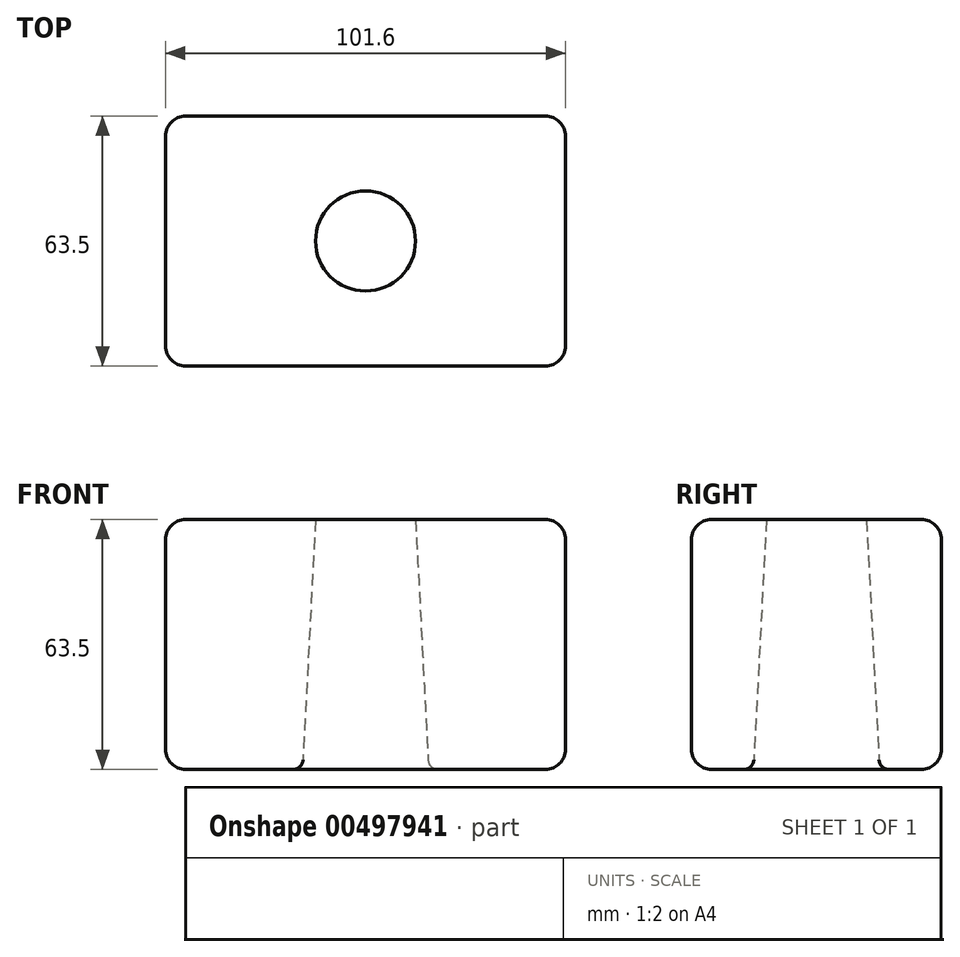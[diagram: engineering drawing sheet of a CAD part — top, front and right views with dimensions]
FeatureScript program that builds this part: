
annotation { "Feature Type Name" : "Feature", "Feature Type Description" : "" }
export const myFeature = defineFeature(function(context is Context, id is Id, definition is map)
    precondition{}
    {
        {
            var Q0;
            Q0=qCreatedBy(makeId("Top.planeOp"),FACE);
            var sketch = newSketch(context, id + "F0", { "sketchPlane" : qUnion([Q0])});
            skLineSegment(sketch, "E0.bottom", {"start": v(50.8, 31.75) * mm, "end": v(-50.8, 31.75) * mm});
            skLineSegment(sketch, "E0.top", {"start": v(50.8, -31.75) * mm, "end": v(-50.8, -31.75) * mm});
            skLineSegment(sketch, "E0.left", {"start": v(50.8, 31.75) * mm, "end": v(50.8, -31.75) * mm});
            skLineSegment(sketch, "E0.right", {"start": v(-50.8, 31.75) * mm, "end": v(-50.8, -31.75) * mm});
            skPoint(sketch, "E0.middle", {"position": v(0, 0) * mm});
            skSolve(sketch);
        }
        {
            var Q0;
            Q0 = qSketchRegion(id + "F0", true);
            extrude(context, id + "F1", {"entities" : qUnion([Q0]), "endBound" : BoundingType.SYMMETRIC, "depth" : 63.5 * mm});
        }
        {
            var Q0;
            Q0=makeQuery(id+"F1.opExtrude","CAP_FACE",FACE,{"disambiguationData":[OSD([sQuery(id+"F0.wireOp",EDGE,"E0.bottom"),sQuery(id+"F0.wireOp",EDGE,"E0.top"),sQuery(id+"F0.wireOp",EDGE,"E0.left"),sQuery(id+"F0.wireOp",EDGE,"E0.right"),sQuery(id+"F0.wireOp",EDGE,"gUM4WlBC-VqhS-AEsS-gTAw-i3EQ8ykjMu5x")])],"isStart":false});
            var Q1;
            Q1=makeQuery(id+"F1.opExtrude","SWEPT_FACE",FACE,{"disambiguationData":[OSD([sQuery(id+"F0.wireOp",EDGE,"E0.top")])]});
            var Q2;
            Q2=makeQuery(id+"F1.opExtrude","SWEPT_FACE",FACE,{"disambiguationData":[OSD([sQuery(id+"F0.wireOp",EDGE,"E0.right")])]});
            var Q3;
            Q3=makeQuery(id+"F1.opExtrude","CAP_FACE",FACE,{"disambiguationData":[OSD([sQuery(id+"F0.wireOp",EDGE,"E0.bottom"),sQuery(id+"F0.wireOp",EDGE,"E0.top"),sQuery(id+"F0.wireOp",EDGE,"E0.left"),sQuery(id+"F0.wireOp",EDGE,"E0.right"),sQuery(id+"F0.wireOp",EDGE,"gUM4WlBC-VqhS-AEsS-gTAw-i3EQ8ykjMu5x")])],"isStart":true});
            var Q4;
            Q4=makeQuery(id+"F1.opExtrude","SWEPT_FACE",FACE,{"disambiguationData":[OSD([sQuery(id+"F0.wireOp",EDGE,"E0.left")])]});
            fillet(context, id + "F2", {"entities" : qUnion([Q0, Q1, Q2, Q3, Q4]), "radius" : 5.08 * mm, "tangentPropagation" : true, "allowEdgeOverflow" : false});
        }
        {
            var Q0;
            Q0=makeQuery(id+"F1.opExtrude","CAP_FACE",FACE,{"disambiguationData":[OSD([sQuery(id+"F0.wireOp",EDGE,"E0.bottom"),sQuery(id+"F0.wireOp",EDGE,"E0.top"),sQuery(id+"F0.wireOp",EDGE,"E0.left"),sQuery(id+"F0.wireOp",EDGE,"E0.right")])],"isStart":false});
            var sketch = newSketch(context, id + "F3", { "sketchPlane" : qUnion([Q0])});
            skCircle(sketch, "E1", {"center": v(0, 0) * mm, "radius": 12.7 * mm});
            skSolve(sketch);
        }
        {
            var Q0;
            Q0 = qSketchRegion(id + "F3", true);
            extrude(context, id + "F4", {"entities" : qUnion([Q0]), "operationType" : NewBodyOperationType.REMOVE, "oppositeDirection" : true, "depth" : 86.87 * mm, "hasDraft" : true, "draftAngle" : 3 * degree});
        }
        {
            var Q0;
            Q0=makeQuery(id+"F4.boolean.opBoolean","COPY",EDGE,{"derivedFrom":makeQuery(id+"F4.opExtrude","CAP_EDGE",EDGE,{"disambiguationData":[OSD([sQuery(id+"F3.wireOp",EDGE,"E1")])],"isStart":true})});
            var Q1;
            Q1=makeQuery(id+"F4.boolean.opBoolean","INTERSECT",EDGE,{"derivedFrom":[makeQuery(id+"F1.opExtrude","CAP_FACE",FACE,{"disambiguationData":[OSD([sQuery(id+"F0.wireOp",EDGE,"E0.bottom"),sQuery(id+"F0.wireOp",EDGE,"E0.top"),sQuery(id+"F0.wireOp",EDGE,"E0.left"),sQuery(id+"F0.wireOp",EDGE,"E0.right")])],"isStart":true}),makeQuery(id+"F4.opExtrude","SWEPT_FACE",FACE,{"disambiguationData":[OSD([sQuery(id+"F3.wireOp",EDGE,"E1")])]})]});
            fillet(context, id + "F5", {"entities" : qUnion([Q0, Q1]), "radius" : 2.54 * mm, "tangentPropagation" : true, "allowEdgeOverflow" : false});
        }
    });
